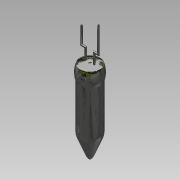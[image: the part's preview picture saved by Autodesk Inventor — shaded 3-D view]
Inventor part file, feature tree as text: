
AUTODESK INVENTOR PART (.ipt)
format: ipt  version: 2015 SP1 (Build 190203100, 203)  size: 943,616 bytes
history: native  units: mm
features: sketch x3, sweep x2, projected_geometry x2, revolve x1, plane x1
ambient origin geometry x8: Origin, YZ Plane, XZ Plane, XY Plane, X Axis, Y Axis, Z Axis, Center Point
bodies: Solid1 (feature_tree)
feature tree (9):
  revolve  "Revolution1"  [1 undecoded]
  sketch  "Sketch2"  dims[d9=0.5mm d10=5.0mm]
  plane  "Work Plane1"
  sketch  "Sketch3"  dims[d11=90.0deg d15=10.026647mm d16=2.0mm d19=5.0mm d20=0.0mm d21=2.0mm d22=90.0deg d23=12.0mm d24=90.0deg d25=5.0mm d26=0.0mm d27=2.0mm d28=90.0deg d29=8.0mm d30=24.25mm d31=0.9mm d32=0.9mm d33=0.0mm d34=0.0mm d35=0.0mm d36=0.0mm]
  sweep  "Sweep1"
  sweep  "Sweep2"
  sketch  "Sketch1"  dims[d6=7.0mm d7=4.75mm]
  projected_geometry  "Projected Loop1"
  projected_geometry  "Projected Loop2"
note: 1 required parameter value undecoded (feature->parameter linkage not recoverable at this tier; creation-order binding heuristic only, values carry confidence <= 0.55)
